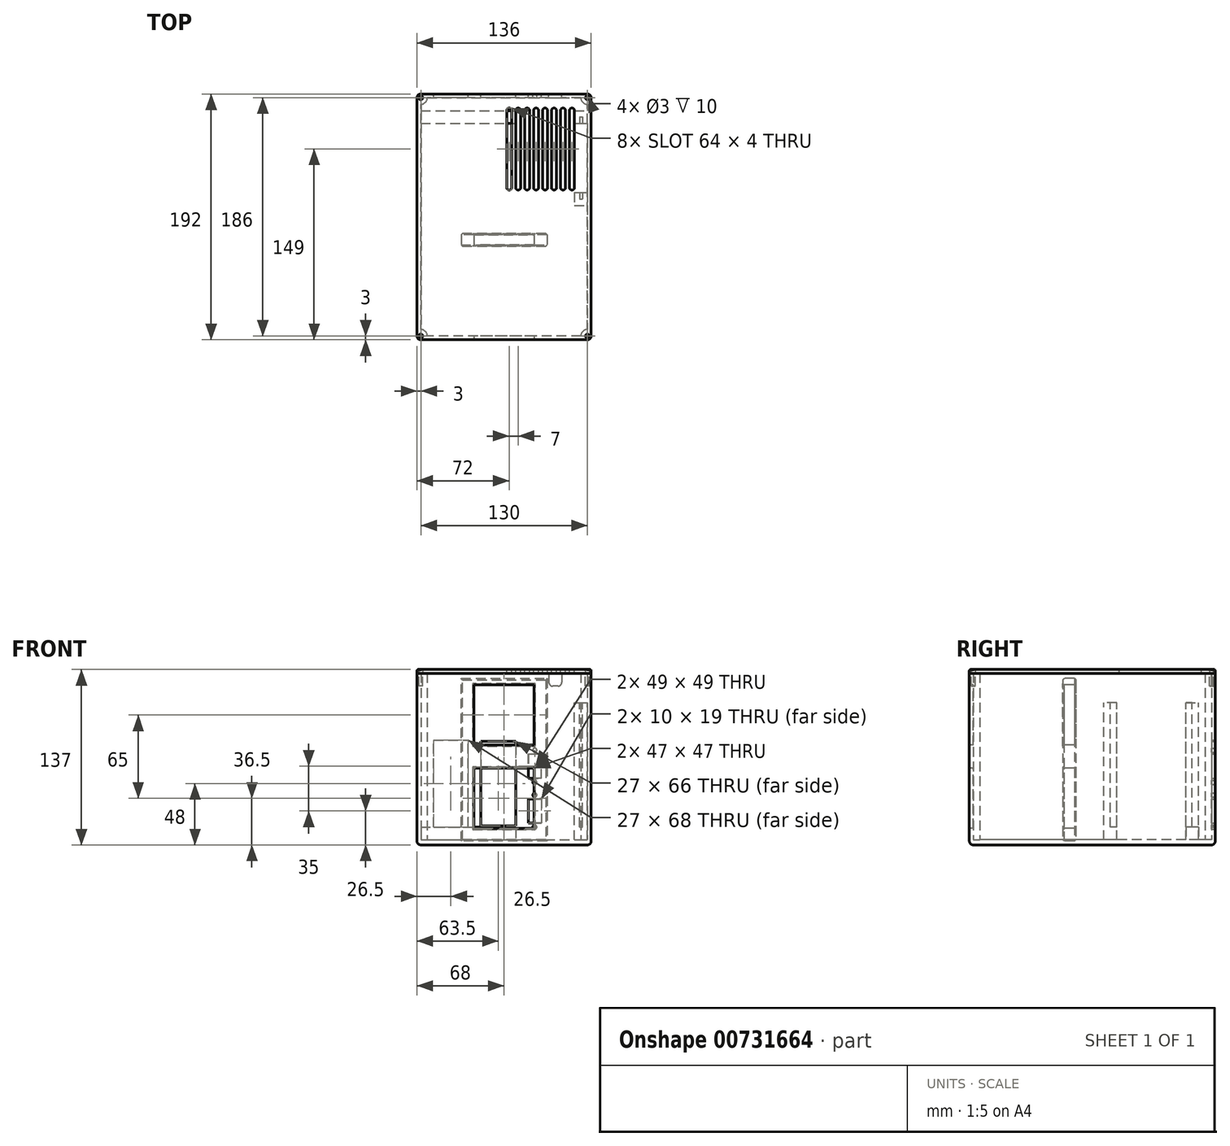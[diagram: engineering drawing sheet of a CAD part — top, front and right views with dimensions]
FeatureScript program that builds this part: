
annotation { "Feature Type Name" : "Feature", "Feature Type Description" : "" }
export const myFeature = defineFeature(function(context is Context, id is Id, definition is map)
    precondition{}
    {
        {
            var Q0;
            Q0=qCreatedBy(makeId("Top.planeOp"),FACE);
            var sketch = newSketch(context, id + "F0", { "sketchPlane" : qUnion([Q0])});
            skLineSegment(sketch, "E0.bottom", {"start": v(60, -93) * mm, "end": v(-60, -93) * mm});
            skLineSegment(sketch, "E0.top", {"start": v(60, 93) * mm, "end": v(-60, 93) * mm});
            skLineSegment(sketch, "E0.left", {"start": v(65, -88) * mm, "end": v(65, 88) * mm});
            skLineSegment(sketch, "E0.right", {"start": v(-65, -88) * mm, "end": v(-65, 88) * mm});
            skPoint(sketch, "E0.middle", {"position": v(0, 0) * mm});
            skLineSegment(sketch, "E1.bottom", {"start": v(68, -96) * mm, "end": v(-68, -96) * mm});
            skLineSegment(sketch, "E1.top", {"start": v(68, 96) * mm, "end": v(-68, 96) * mm});
            skLineSegment(sketch, "E1.left", {"start": v(68, -96) * mm, "end": v(68, 96) * mm});
            skLineSegment(sketch, "E1.right", {"start": v(-68, -96) * mm, "end": v(-68, 96) * mm});
            skArc(sketch, "E2", {"start": v(65, 88) * mm, "mid": v(61.46, 89.46) * mm, "end": v(60, 93) * mm});
            skArc(sketch, "E3.MirrorCS", {"start": v(65, -88) * mm, "mid": v(61.46, -89.46) * mm, "end": v(60, -93) * mm});
            skArc(sketch, "E4.MirrorCS", {"start": v(-65, -88) * mm, "mid": v(-61.46, -89.46) * mm, "end": v(-60, -93) * mm});
            skArc(sketch, "E5.MirrorCS", {"start": v(-65, 88) * mm, "mid": v(-61.46, 89.46) * mm, "end": v(-60, 93) * mm});
            skSolve(sketch);
        }
        {
            var Q0;
            Q0=makeQuery(id+"F0.imprint","IMPRINT",FACE,{"disambiguationData":[TD([[makeQuery(id+"F0.imprint","IMPRINT",EDGE,{"derivedFrom":sQuery(id+"F0.wireOp",EDGE,"E0.bottom")}),-1.0]])]});
            var Q1;
            Q1=makeQuery(id+"F0.imprint","IMPRINT",FACE,{"disambiguationData":[TD([[makeQuery(id+"F0.imprint","IMPRINT",EDGE,{"derivedFrom":sQuery(id+"F0.wireOp",EDGE,"E0.bottom")}),1.0]])]});
            extrude(context, id + "F1", {"entities" : qUnion([Q0, Q1]), "depth" : 4 * mm, "offsetDistance" : 25 * mm});
        }
        {
            var Q0;
            Q0=makeQuery(id+"F0.imprint","IMPRINT",FACE,{"disambiguationData":[TD([[makeQuery(id+"F0.imprint","IMPRINT",EDGE,{"derivedFrom":sQuery(id+"F0.wireOp",EDGE,"E0.bottom")}),1.0]])]});
            extrude(context, id + "F2", {"entities" : qUnion([Q0]), "operationType" : NewBodyOperationType.ADD, "depth" : 134 * mm, "offsetDistance" : 25 * mm});
        }
        {
            var Q0;
            {var subQ0=sQuery(id+"F0.wireOp",EDGE,"E1.bottom");Q0=makeQuery(id+"F2.boolean.opBoolean","MERGE",FACE,{"derivedFrom":[makeQuery(id+"F1.opExtrude","SWEPT_FACE",FACE,{"disambiguationData":[OSD([subQ0])]}),makeQuery(id+"F2.opExtrude","SWEPT_FACE",FACE,{"disambiguationData":[OSD([subQ0])]})]});}
            var sketch = newSketch(context, id + "F3", { "sketchPlane" : qUnion([Q0])});
            skLineSegment(sketch, "E6.bottom", {"start": v(23.5, 78) * mm, "end": v(-23.5, 78) * mm});
            skLineSegment(sketch, "E6.top", {"start": v(23.5, 125) * mm, "end": v(-23.5, 125) * mm});
            skLineSegment(sketch, "E6.left", {"start": v(23.5, 78) * mm, "end": v(23.5, 125) * mm});
            skLineSegment(sketch, "E6.right", {"start": v(-23.5, 78) * mm, "end": v(-23.5, 125) * mm});
            skPoint(sketch, "E6.middle", {"position": v(0, 101.5) * mm});
            skLineSegment(sketch, "E7.bottom", {"start": v(23.5, 13) * mm, "end": v(-23.5, 13) * mm});
            skLineSegment(sketch, "E7.top", {"start": v(23.5, 60) * mm, "end": v(-23.5, 60) * mm});
            skLineSegment(sketch, "E7.left", {"start": v(23.5, 13) * mm, "end": v(23.5, 60) * mm});
            skLineSegment(sketch, "E7.right", {"start": v(-23.5, 13) * mm, "end": v(-23.5, 60) * mm});
            skPoint(sketch, "E7.middle", {"position": v(0, 36.5) * mm});
            skSolve(sketch);
        }
        {
            var Q0;
            Q0=makeQuery(id+"F3.imprint","IMPRINT",FACE,{"disambiguationData":[TD([[makeQuery(id+"F3.imprint","IMPRINT",EDGE,{"derivedFrom":sQuery(id+"F3.wireOp",EDGE,"E6.bottom")}),-1.0]])]});
            var Q1;
            Q1=makeQuery(id+"F3.imprint","IMPRINT",FACE,{"disambiguationData":[TD([[makeQuery(id+"F3.imprint","IMPRINT",EDGE,{"derivedFrom":sQuery(id+"F3.wireOp",EDGE,"E7.bottom")}),-1.0]])]});
            extrude(context, id + "F4", {"entities" : qUnion([Q0, Q1]), "operationType" : NewBodyOperationType.REMOVE, "oppositeDirection" : true, "depth" : 25 * mm, "offsetDistance" : 25 * mm});
        }
        {
            var Q0;
            Q0=makeQuery(id+"F1.opExtrude","CAP_FACE",FACE,{"disambiguationData":[OSD([sQuery(id+"F0.wireOp",EDGE,"E1.bottom"),sQuery(id+"F0.wireOp",EDGE,"E1.top"),sQuery(id+"F0.wireOp",EDGE,"E1.left"),sQuery(id+"F0.wireOp",EDGE,"E1.right")])],"isStart":false});
            var sketch = newSketch(context, id + "F5", { "sketchPlane" : qUnion([Q0])});
            skLineSegment(sketch, "E8.bottom", {"start": v(-65, 73) * mm, "end": v(19, 73) * mm});
            skLineSegment(sketch, "E8.top", {"start": v(-65, 83) * mm, "end": v(19, 83) * mm});
            skLineSegment(sketch, "E8.left", {"start": v(-65, 73) * mm, "end": v(-65, 83) * mm});
            skLineSegment(sketch, "E8.right", {"start": v(19, 73) * mm, "end": v(19, 83) * mm});
            skSolve(sketch);
        }
        {
            var Q0;
            Q0=makeQuery(id+"F5.imprint","IMPRINT",FACE,{"disambiguationData":[TD([[makeQuery(id+"F5.imprint","IMPRINT",EDGE,{"derivedFrom":sQuery(id+"F5.wireOp",EDGE,"E8.bottom")}),1.0]])]});
            extrude(context, id + "F6", {"entities" : qUnion([Q0]), "operationType" : NewBodyOperationType.ADD, "depth" : 20 * mm, "offsetDistance" : 25 * mm});
        }
        {
            var Q0;
            Q0=makeQuery(id+"F6.opExtrude","SWEPT_FACE",FACE,{"disambiguationData":[OSD([sQuery(id+"F5.wireOp",EDGE,"E8.bottom")])]});
            var sketch = newSketch(context, id + "F7", { "sketchPlane" : qUnion([Q0])});
            skLineSegment(sketch, "E9", {"start": v(-18, 14) * mm, "end": v(9, 14) * mm});
            skLineSegment(sketch, "E10", {"start": v(-28, 14) * mm, "end": v(-55, 14) * mm});
            skLineSegment(sketch, "E11", {"start": v(-55, 33.64) * mm, "end": v(19, 33.64) * mm});
            skLineSegment(sketch, "E12", {"start": v(19, 33.64) * mm, "end": v(19, 24) * mm});
            skLineSegment(sketch, "E13", {"start": v(-28, 14) * mm, "end": v(-18, 14) * mm});
            skLineSegment(sketch, "E14.0.0", {"start": v(9, 4) * mm, "end": v(19, 4) * mm});
            skLineSegment(sketch, "E14.0.1", {"start": v(19, 4) * mm, "end": v(19, 24) * mm});
            skLineSegment(sketch, "E14.0.3", {"start": v(-65, 24) * mm, "end": v(-65, 14) * mm});
            skLineSegment(sketch, "E15", {"start": v(9, 14) * mm, "end": v(9, 4) * mm});
            skLineSegment(sketch, "E16", {"start": v(-55, 14) * mm, "end": v(-65, 14) * mm});
            skLineSegment(sketch, "E17", {"start": v(-65, 24) * mm, "end": v(-65, 33.64) * mm});
            skLineSegment(sketch, "E18", {"start": v(-65, 33.64) * mm, "end": v(-55, 33.64) * mm});
            skPoint(sketch, "E19.orphan", {"position": v(-65, 4) * mm});
            skSolve(sketch);
        }
        {
            var Q0;
            Q0=qSketchRegion(id+"F7",true);
            extrude(context, id + "F8", {"entities" : qUnion([Q0]), "operationType" : NewBodyOperationType.REMOVE, "oppositeDirection" : true, "depth" : 10 * mm, "offsetDistance" : 25 * mm});
        }
        {
            var Q0;
            Q0=makeQuery(id+"F2.opExtrude","SWEPT_FACE",FACE,{"disambiguationData":[OSD([sQuery(id+"F0.wireOp",EDGE,"E0.left")])]});
            var sketch = newSketch(context, id + "F9", { "sketchPlane" : qUnion([Q0])});
            skLineSegment(sketch, "E20.bottom", {"start": v(-73, 4) * mm, "end": v(-83, 4) * mm});
            skLineSegment(sketch, "E20.top", {"start": v(-73, 111) * mm, "end": v(-83, 111) * mm});
            skLineSegment(sketch, "E20.left", {"start": v(-73, 4) * mm, "end": v(-73, 111) * mm});
            skLineSegment(sketch, "E20.right", {"start": v(-83, 4) * mm, "end": v(-83, 111) * mm});
            skLineSegment(sketch, "E21.bottom", {"start": v(-19, 4) * mm, "end": v(-9, 4) * mm});
            skLineSegment(sketch, "E21.top", {"start": v(-19, 111) * mm, "end": v(-9, 111) * mm});
            skLineSegment(sketch, "E21.left", {"start": v(-19, 4) * mm, "end": v(-19, 111) * mm});
            skLineSegment(sketch, "E21.right", {"start": v(-9, 4) * mm, "end": v(-9, 111) * mm});
            skPoint(sketch, "E22.centerSnap0", {"position": v(-78, 111) * mm});
            skPoint(sketch, "E23.centerSnap0", {"position": v(-14, 111) * mm});
            skPoint(sketch, "E24.centerSnap0", {"position": v(-78, 4) * mm});
            skSolve(sketch);
        }
        {
            var Q0;
            Q0=qSketchRegion(id+"F9",true);
            extrude(context, id + "F10", {"entities" : qUnion([Q0]), "operationType" : NewBodyOperationType.ADD, "depth" : 10 * mm, "offsetDistance" : 25 * mm});
        }
        {
            var Q0;
            Q0=makeQuery(id+"F2.opExtrude","CAP_FACE",FACE,{"disambiguationData":[OSD([sQuery(id+"F0.wireOp",EDGE,"E0.bottom"),sQuery(id+"F0.wireOp",EDGE,"E0.top"),sQuery(id+"F0.wireOp",EDGE,"E0.left"),sQuery(id+"F0.wireOp",EDGE,"E0.right"),sQuery(id+"F0.wireOp",EDGE,"E1.bottom"),sQuery(id+"F0.wireOp",EDGE,"E1.top"),sQuery(id+"F0.wireOp",EDGE,"E1.left"),sQuery(id+"F0.wireOp",EDGE,"E1.right"),sQuery(id+"F0.wireOp",EDGE,"E2"),sQuery(id+"F0.wireOp",EDGE,"E3.MirrorCS"),sQuery(id+"F0.wireOp",EDGE,"E4.MirrorCS"),sQuery(id+"F0.wireOp",EDGE,"E5.MirrorCS")])],"isStart":false});
            var sketch = newSketch(context, id + "F11", { "sketchPlane" : qUnion([Q0])});
            skCircle(sketch, "E25", {"center": v(65, 93) * mm, "radius": 1.5 * mm});
            skCircle(sketch, "E26", {"center": v(-65, 93) * mm, "radius": 1.5 * mm});
            skCircle(sketch, "E27", {"center": v(65, -93) * mm, "radius": 1.5 * mm});
            skCircle(sketch, "E28", {"center": v(-65, -93) * mm, "radius": 1.5 * mm});
            skSolve(sketch);
        }
        {
            var Q0;
            Q0=qSketchRegion(id+"F11",true);
            extrude(context, id + "F12", {"entities" : qUnion([Q0]), "operationType" : NewBodyOperationType.REMOVE, "oppositeDirection" : true, "depth" : 10 * mm, "offsetDistance" : 25 * mm});
        }
        {
            var Q0;
            {var subQ0=sQuery(id+"F0.wireOp",EDGE,"E1.top");Q0=makeQuery(id+"F2.boolean.opBoolean","MERGE",FACE,{"derivedFrom":[makeQuery(id+"F1.opExtrude","SWEPT_FACE",FACE,{"disambiguationData":[OSD([subQ0])]}),makeQuery(id+"F2.opExtrude","SWEPT_FACE",FACE,{"disambiguationData":[OSD([subQ0])]})]});}
            var sketch = newSketch(context, id + "F13", { "sketchPlane" : qUnion([Q0])});
            skLineSegment(sketch, "E29.bottom", {"start": v(55, 14) * mm, "end": v(28, 14) * mm});
            skLineSegment(sketch, "E29.top", {"start": v(55, 82) * mm, "end": v(28, 82) * mm});
            skLineSegment(sketch, "E29.left", {"start": v(55, 14) * mm, "end": v(55, 82) * mm});
            skLineSegment(sketch, "E29.right", {"start": v(28, 14) * mm, "end": v(28, 82) * mm});
            skPoint(sketch, "E29.middle", {"position": v(41.5, 48) * mm});
            skLineSegment(sketch, "E30.bottom", {"start": v(18, 15) * mm, "end": v(-9, 15) * mm});
            skLineSegment(sketch, "E30.top", {"start": v(18, 81) * mm, "end": v(-9, 81) * mm});
            skLineSegment(sketch, "E30.left", {"start": v(18, 15) * mm, "end": v(18, 81) * mm});
            skLineSegment(sketch, "E30.right", {"start": v(-9, 15) * mm, "end": v(-9, 81) * mm});
            skPoint(sketch, "E30.middle", {"position": v(4.5, 48) * mm});
            skLineSegment(sketch, "E31.bottom", {"start": v(-45, 134) * mm, "end": v(-35, 134) * mm});
            skLineSegment(sketch, "E31.top", {"start": v(-45, 124) * mm, "end": v(-35, 124) * mm});
            skLineSegment(sketch, "E31.left", {"start": v(-45, 134) * mm, "end": v(-45, 124) * mm});
            skLineSegment(sketch, "E31.right", {"start": v(-35, 134) * mm, "end": v(-35, 124) * mm});
            skLineSegment(sketch, "E32.bottom", {"start": v(-29, 36) * mm, "end": v(-19, 36) * mm});
            skLineSegment(sketch, "E32.top", {"start": v(-29, 17) * mm, "end": v(-19, 17) * mm});
            skLineSegment(sketch, "E32.left", {"start": v(-29, 36) * mm, "end": v(-29, 17) * mm});
            skLineSegment(sketch, "E32.right", {"start": v(-19, 36) * mm, "end": v(-19, 17) * mm});
            skCircle(sketch, "E33", {"center": v(-24, 14) * mm, "radius": 1.6 * mm});
            skPoint(sketch, "E33.centerSnap0", {"position": v(-24, 17) * mm});
            skCircle(sketch, "E34", {"center": v(-24, 39) * mm, "radius": 1.6 * mm});
            skPoint(sketch, "E34.centerSnap0", {"position": v(-24, 36) * mm});
            skCircle(sketch, "E35", {"center": v(-24, 49) * mm, "radius": 1.6 * mm});
            skLineSegment(sketch, "E36.bottom", {"start": v(-19, 52) * mm, "end": v(-29, 52) * mm});
            skLineSegment(sketch, "E36.top", {"start": v(-19, 71) * mm, "end": v(-29, 71) * mm});
            skLineSegment(sketch, "E36.left", {"start": v(-19, 52) * mm, "end": v(-19, 71) * mm});
            skLineSegment(sketch, "E36.right", {"start": v(-29, 52) * mm, "end": v(-29, 71) * mm});
            skCircle(sketch, "E37", {"center": v(-24, 74) * mm, "radius": 1.6 * mm});
            skSolve(sketch);
        }
        {
            var Q0;
            Q0=makeQuery(id+"F13.imprint","IMPRINT",FACE,{"disambiguationData":[TD([[makeQuery(id+"F13.imprint","IMPRINT",EDGE,{"derivedFrom":sQuery(id+"F13.wireOp",EDGE,"E31.bottom")}),-1.0]])]});
            var Q1;
            Q1=qSketchRegion(id+"F13",true);
            extrude(context, id + "F14", {"entities" : qUnion([Q0, Q1]), "operationType" : NewBodyOperationType.REMOVE, "oppositeDirection" : true, "depth" : 25 * mm, "offsetDistance" : 25 * mm});
        }
        {
            var Q0;
            {var subQ0=sQuery(id+"F0.wireOp",EDGE,"E1.right");var subQ1=sQuery(id+"F0.wireOp",EDGE,"E1.bottom");Q0=makeQuery(id+"F2.boolean.opBoolean","MERGE",EDGE,{"derivedFrom":[makeQuery(id+"F1.opExtrude","SWEPT_EDGE",EDGE,{"disambiguationData":[OSD([subQ1,subQ0])]}),makeQuery(id+"F2.opExtrude","SWEPT_EDGE",EDGE,{"disambiguationData":[OSD([subQ1,subQ0])]})]});}
            var Q1;
            {var subQ0=sQuery(id+"F0.wireOp",EDGE,"E1.left");var subQ1=sQuery(id+"F0.wireOp",EDGE,"E1.bottom");Q1=makeQuery(id+"F2.boolean.opBoolean","MERGE",EDGE,{"derivedFrom":[makeQuery(id+"F1.opExtrude","SWEPT_EDGE",EDGE,{"disambiguationData":[OSD([subQ1,subQ0])]}),makeQuery(id+"F2.opExtrude","SWEPT_EDGE",EDGE,{"disambiguationData":[OSD([subQ1,subQ0])]})]});}
            var Q2;
            {var subQ0=sQuery(id+"F0.wireOp",EDGE,"E1.left");var subQ1=sQuery(id+"F0.wireOp",EDGE,"E1.top");Q2=makeQuery(id+"F2.boolean.opBoolean","MERGE",EDGE,{"derivedFrom":[makeQuery(id+"F1.opExtrude","SWEPT_EDGE",EDGE,{"disambiguationData":[OSD([subQ1,subQ0])]}),makeQuery(id+"F2.opExtrude","SWEPT_EDGE",EDGE,{"disambiguationData":[OSD([subQ1,subQ0])]})]});}
            var Q3;
            {var subQ0=sQuery(id+"F0.wireOp",EDGE,"E1.right");var subQ1=sQuery(id+"F0.wireOp",EDGE,"E1.top");Q3=makeQuery(id+"F2.boolean.opBoolean","MERGE",EDGE,{"derivedFrom":[makeQuery(id+"F1.opExtrude","SWEPT_EDGE",EDGE,{"disambiguationData":[OSD([subQ1,subQ0])]}),makeQuery(id+"F2.opExtrude","SWEPT_EDGE",EDGE,{"disambiguationData":[OSD([subQ1,subQ0])]})]});}
            fillet(context, id + "F15", {"entities" : qUnion([Q0, Q1, Q2, Q3]), "radius" : 3 * mm, "tangentPropagation" : true, "allowEdgeOverflow" : false});
        }
        {
            var Q0;
            Q0=makeQuery(id+"F1.opExtrude","CAP_EDGE",EDGE,{"disambiguationData":[OSD([sQuery(id+"F0.wireOp",EDGE,"E1.bottom")])],"isStart":true});
            fillet(context, id + "F16", {"entities" : qUnion([Q0]), "radius" : 3 * mm, "tangentPropagation" : true, "allowEdgeOverflow" : false});
        }
        {
            var Q0;
            Q0=makeQuery(id+"F14.boolean.opBoolean","COPY",EDGE,{"derivedFrom":makeQuery(id+"F14.opExtrude","SWEPT_EDGE",EDGE,{"disambiguationData":[OSD([sQuery(id+"F13.wireOp",EDGE,"E31.top"),sQuery(id+"F13.wireOp",EDGE,"E31.left")])]})});
            var Q1;
            Q1=makeQuery(id+"F14.boolean.opBoolean","COPY",EDGE,{"derivedFrom":makeQuery(id+"F14.opExtrude","SWEPT_EDGE",EDGE,{"disambiguationData":[OSD([sQuery(id+"F13.wireOp",EDGE,"E31.top"),sQuery(id+"F13.wireOp",EDGE,"E31.right")])]})});
            fillet(context, id + "F17", {"entities" : qUnion([Q0, Q1]), "radius" : 3 * mm, "tangentPropagation" : true, "allowEdgeOverflow" : false});
        }
        {
            var Q0;
            Q0=makeQuery(id+"F2.opExtrude","SWEPT_FACE",FACE,{"disambiguationData":[OSD([sQuery(id+"F0.wireOp",EDGE,"E0.bottom")])]});
            cPlane(context, id + "F18", {"entities" : qUnion([Q0]), "cplaneType" : CPlaneType.OFFSET, "offset" : 70 * mm, "width" : 150 * mm, "height" : 150 * mm});
        }
        {
            var Q0;
            Q0=qCreatedBy(id+"F18.planeOp",FACE);
            var sketch = newSketch(context, id + "F19", { "sketchPlane" : qUnion([Q0])});
            skLineSegment(sketch, "E38.0", {"start": v(-23.5, 125) * mm, "end": v(23.5, 125) * mm});
            skLineSegment(sketch, "E39.0", {"start": v(-23.5, 78) * mm, "end": v(-23.5, 125) * mm});
            skLineSegment(sketch, "E40.0", {"start": v(23.5, 78) * mm, "end": v(23.5, 125) * mm});
            skLineSegment(sketch, "E41.0", {"start": v(-23.5, 78) * mm, "end": v(23.5, 78) * mm});
            skLineSegment(sketch, "E42.0", {"start": v(-23.5, 60) * mm, "end": v(23.5, 60) * mm});
            skLineSegment(sketch, "E43.0", {"start": v(23.5, 13) * mm, "end": v(23.5, 60) * mm});
            skLineSegment(sketch, "E44.0", {"start": v(-23.5, 13) * mm, "end": v(23.5, 13) * mm});
            skLineSegment(sketch, "E45.0", {"start": v(-23.5, 13) * mm, "end": v(-23.5, 60) * mm});
            skLineSegment(sketch, "E46.top", {"start": v(33.5, 130) * mm, "end": v(-33.5, 130) * mm});
            skLineSegment(sketch, "E46.left", {"start": v(33.5, 3) * mm, "end": v(33.5, 130) * mm});
            skLineSegment(sketch, "E46.right", {"start": v(-33.5, 3) * mm, "end": v(-33.5, 130) * mm});
            skLineSegment(sketch, "E47", {"start": v(-33.5, 3) * mm, "end": v(33.5, 3) * mm});
            skSolve(sketch);
        }
        {
            var Q0;
            Q0=makeQuery(id+"F19.imprint","IMPRINT",FACE,{"disambiguationData":[TD([[makeQuery(id+"F19.imprint","IMPRINT",EDGE,{"derivedFrom":sQuery(id+"F19.wireOp",EDGE,"E38.0")}),1.0]])]});
            extrude(context, id + "F20", {"entities" : qUnion([Q0]), "depth" : 10 * mm, "offsetDistance" : 25 * mm});
        }
        {
            var Q0;
            Q0=makeQuery(id+"F20.opExtrude","CAP_FACE",FACE,{"disambiguationData":[OSD([sQuery(id+"F19.wireOp",EDGE,"E38.0"),sQuery(id+"F19.wireOp",EDGE,"E39.0"),sQuery(id+"F19.wireOp",EDGE,"E40.0"),sQuery(id+"F19.wireOp",EDGE,"E41.0"),sQuery(id+"F19.wireOp",EDGE,"E42.0"),sQuery(id+"F19.wireOp",EDGE,"E43.0"),sQuery(id+"F19.wireOp",EDGE,"E44.0"),sQuery(id+"F19.wireOp",EDGE,"E45.0"),sQuery(id+"F19.wireOp",EDGE,"E46.top"),sQuery(id+"F19.wireOp",EDGE,"E46.left"),sQuery(id+"F19.wireOp",EDGE,"E46.right"),sQuery(id+"F19.wireOp",EDGE,"E47")])],"isStart":true});
            var Q1;
            Q1=makeQuery(id+"F20.opExtrude","CAP_FACE",FACE,{"disambiguationData":[OSD([sQuery(id+"F19.wireOp",EDGE,"E38.0"),sQuery(id+"F19.wireOp",EDGE,"E39.0"),sQuery(id+"F19.wireOp",EDGE,"E40.0"),sQuery(id+"F19.wireOp",EDGE,"E41.0"),sQuery(id+"F19.wireOp",EDGE,"E42.0"),sQuery(id+"F19.wireOp",EDGE,"E43.0"),sQuery(id+"F19.wireOp",EDGE,"E44.0"),sQuery(id+"F19.wireOp",EDGE,"E45.0"),sQuery(id+"F19.wireOp",EDGE,"E46.top"),sQuery(id+"F19.wireOp",EDGE,"E46.left"),sQuery(id+"F19.wireOp",EDGE,"E46.right"),sQuery(id+"F19.wireOp",EDGE,"E47")])],"isStart":false});
            chamfer(context, id + "F21", {"entities" : qUnion([Q0, Q1]), "width" : 1 * mm, "tangentPropagation" : true});
        }
        {
            var Q0;
            Q0=makeQuery(id+"F2.opExtrude","CAP_FACE",FACE,{"disambiguationData":[OSD([sQuery(id+"F0.wireOp",EDGE,"E0.bottom"),sQuery(id+"F0.wireOp",EDGE,"E0.top"),sQuery(id+"F0.wireOp",EDGE,"E0.left"),sQuery(id+"F0.wireOp",EDGE,"E0.right"),sQuery(id+"F0.wireOp",EDGE,"E1.bottom"),sQuery(id+"F0.wireOp",EDGE,"E1.top"),sQuery(id+"F0.wireOp",EDGE,"E1.left"),sQuery(id+"F0.wireOp",EDGE,"E1.right"),sQuery(id+"F0.wireOp",EDGE,"E2"),sQuery(id+"F0.wireOp",EDGE,"E3.MirrorCS"),sQuery(id+"F0.wireOp",EDGE,"E4.MirrorCS"),sQuery(id+"F0.wireOp",EDGE,"E5.MirrorCS")])],"isStart":false});
            cPlane(context, id + "F22", {"entities" : qUnion([Q0]), "cplaneType" : CPlaneType.OFFSET, "offset" : 0 * mm, "width" : 150 * mm, "height" : 150 * mm});
        }
        {
            var Q0;
            Q0=qCreatedBy(id+"F22.planeOp",FACE);
            var sketch = newSketch(context, id + "F23", { "sketchPlane" : qUnion([Q0])});
            skLineSegment(sketch, "E48.0.0", {"start": v(68, -93) * mm, "end": v(68, 93) * mm});
            skArc(sketch, "E48.0.1", {"start": v(68, 93) * mm, "mid": v(67.12, 95.12) * mm, "end": v(65, 96) * mm});
            skArc(sketch, "E48.0.5", {"start": v(60, 93) * mm, "mid": v(61.46, 89.46) * mm, "end": v(65, 88) * mm});
            skLineSegment(sketch, "E48.0.6", {"start": v(65, 88) * mm, "end": v(65, -88) * mm});
            skArc(sketch, "E48.0.7", {"start": v(65, -88) * mm, "mid": v(61.46, -89.46) * mm, "end": v(60, -93) * mm});
            skLineSegment(sketch, "E48.0.8", {"start": v(60, -93) * mm, "end": v(-60, -93) * mm});
            skArc(sketch, "E48.0.9", {"start": v(-60, -93) * mm, "mid": v(-61.46, -89.46) * mm, "end": v(-65, -88) * mm});
            skLineSegment(sketch, "E48.0.10", {"start": v(-65, -88) * mm, "end": v(-65, 88) * mm});
            skArc(sketch, "E48.0.11", {"start": v(-65, 88) * mm, "mid": v(-61.46, 89.46) * mm, "end": v(-60, 93) * mm});
            skLineSegment(sketch, "E48.0.12", {"start": v(-60, 93) * mm, "end": v(60, 93) * mm});
            skLineSegment(sketch, "E48.0.14", {"start": v(65, 96) * mm, "end": v(-65, 96) * mm});
            skArc(sketch, "E48.0.15", {"start": v(-65, 96) * mm, "mid": v(-67.12, 95.12) * mm, "end": v(-68, 93) * mm});
            skLineSegment(sketch, "E48.0.16", {"start": v(-68, 93) * mm, "end": v(-68, -93) * mm});
            skArc(sketch, "E48.0.17", {"start": v(-68, -93) * mm, "mid": v(-67.12, -95.12) * mm, "end": v(-65, -96) * mm});
            skLineSegment(sketch, "E48.0.18", {"start": v(-65, -96) * mm, "end": v(65, -96) * mm});
            skArc(sketch, "E48.0.19", {"start": v(65, -96) * mm, "mid": v(67.12, -95.12) * mm, "end": v(68, -93) * mm});
            skPoint(sketch, "E48.0.4.start.orphan", {"position": v(45, 93) * mm});
            skPoint(sketch, "E48.0.2.end.orphan", {"position": v(45, 96) * mm});
            skPoint(sketch, "E49.orphan", {"position": v(35, 93) * mm});
            skPoint(sketch, "E50.orphan", {"position": v(35, 96) * mm});
            skCircle(sketch, "E51.0", {"center": v(65, 93) * mm, "radius": 1.5 * mm});
            skCircle(sketch, "E52.0", {"center": v(-65, 93) * mm, "radius": 1.5 * mm});
            skCircle(sketch, "E53.0", {"center": v(65, -93) * mm, "radius": 1.5 * mm});
            skCircle(sketch, "E54.0", {"center": v(-65, -93) * mm, "radius": 1.5 * mm});
            skLineSegment(sketch, "E55.0", {"start": v(64, -87.08) * mm, "end": v(64, 87.08) * mm});
            skArc(sketch, "E55.1", {"start": v(59.08, -92) * mm, "mid": v(60.76, -88.76) * mm, "end": v(64, -87.08) * mm});
            skArc(sketch, "E55.2", {"start": v(64, 87.08) * mm, "mid": v(60.76, 88.76) * mm, "end": v(59.08, 92) * mm});
            skLineSegment(sketch, "E55.3", {"start": v(-59.08, -92) * mm, "end": v(59.08, -92) * mm});
            skLineSegment(sketch, "E55.4", {"start": v(59.08, 92) * mm, "end": v(-59.08, 92) * mm});
            skArc(sketch, "E55.5", {"start": v(-59.08, 92) * mm, "mid": v(-60.76, 88.76) * mm, "end": v(-64, 87.08) * mm});
            skLineSegment(sketch, "E55.6", {"start": v(-64, 87.08) * mm, "end": v(-64, -87.08) * mm});
            skArc(sketch, "E55.7", {"start": v(-64, -87.08) * mm, "mid": v(-60.76, -88.76) * mm, "end": v(-59.08, -92) * mm});
            skSolve(sketch);
        }
        {
            var Q0;
            Q0=makeQuery(id+"F23.imprint","IMPRINT",FACE,{"disambiguationData":[TD([[makeQuery(id+"F23.imprint","IMPRINT",EDGE,{"derivedFrom":sQuery(id+"F23.wireOp",EDGE,"E48.0.0")}),1.0]])]});
            var Q1;
            Q1=makeQuery(id+"F23.imprint","IMPRINT",FACE,{"disambiguationData":[TD([[makeQuery(id+"F23.imprint","IMPRINT",EDGE,{"derivedFrom":sQuery(id+"F23.wireOp",EDGE,"E48.0.5")}),-1.0]])]});
            var Q2;
            Q2=makeQuery(id+"F23.imprint","IMPRINT",FACE,{"disambiguationData":[TD([[makeQuery(id+"F23.imprint","IMPRINT",EDGE,{"derivedFrom":sQuery(id+"F23.wireOp",EDGE,"E55.0")}),1.0]])]});
            extrude(context, id + "F24", {"entities" : qUnion([Q0, Q1, Q2]), "depth" : 3 * mm, "offsetDistance" : 25 * mm});
        }
        {
            var Q0;
            Q0=makeQuery(id+"F24.opExtrude","CAP_FACE",FACE,{"disambiguationData":[OSD([sQuery(id+"F23.wireOp",EDGE,"E48.0.0"),sQuery(id+"F23.wireOp",EDGE,"E48.0.1"),sQuery(id+"F23.wireOp",EDGE,"E48.0.14"),sQuery(id+"F23.wireOp",EDGE,"E48.0.15"),sQuery(id+"F23.wireOp",EDGE,"E48.0.16"),sQuery(id+"F23.wireOp",EDGE,"E48.0.17"),sQuery(id+"F23.wireOp",EDGE,"E48.0.18"),sQuery(id+"F23.wireOp",EDGE,"E48.0.19"),sQuery(id+"F23.wireOp",EDGE,"E51.0"),sQuery(id+"F23.wireOp",EDGE,"E52.0"),sQuery(id+"F23.wireOp",EDGE,"E53.0"),sQuery(id+"F23.wireOp",EDGE,"E54.0")])],"isStart":false});
            fillet(context, id + "F25", {"entities" : qUnion([Q0]), "radius" : 1 * mm, "tangentPropagation" : true, "allowEdgeOverflow" : false});
        }
        {
            var Q0;
            Q0=makeQuery(id+"F24.opExtrude","CAP_FACE",FACE,{"disambiguationData":[OSD([sQuery(id+"F23.wireOp",EDGE,"E48.0.0"),sQuery(id+"F23.wireOp",EDGE,"E48.0.1"),sQuery(id+"F23.wireOp",EDGE,"E48.0.14"),sQuery(id+"F23.wireOp",EDGE,"E48.0.15"),sQuery(id+"F23.wireOp",EDGE,"E48.0.16"),sQuery(id+"F23.wireOp",EDGE,"E48.0.17"),sQuery(id+"F23.wireOp",EDGE,"E48.0.18"),sQuery(id+"F23.wireOp",EDGE,"E48.0.19"),sQuery(id+"F23.wireOp",EDGE,"E51.0"),sQuery(id+"F23.wireOp",EDGE,"E52.0"),sQuery(id+"F23.wireOp",EDGE,"E53.0"),sQuery(id+"F23.wireOp",EDGE,"E54.0")])],"isStart":false});
            var sketch = newSketch(context, id + "F26", { "sketchPlane" : qUnion([Q0])});
            skLineSegment(sketch, "E56.left", {"start": v(2, 83) * mm, "end": v(2, 23) * mm});
            skLineSegment(sketch, "E56.right", {"start": v(6, 83) * mm, "end": v(6, 23) * mm});
            skArc(sketch, "E57", {"start": v(2, 83) * mm, "mid": v(4, 85) * mm, "end": v(6, 83) * mm});
            skArc(sketch, "E58", {"start": v(2, 23) * mm, "mid": v(4, 21) * mm, "end": v(6, 23) * mm});
            skLineSegment(sketch, "E59.1.0.0", {"start": v(13, 83) * mm, "end": v(13, 23) * mm});
            skLineSegment(sketch, "E59.1.0.1", {"start": v(9, 83) * mm, "end": v(9, 23) * mm});
            skArc(sketch, "E59.1.0.2", {"start": v(9, 83) * mm, "mid": v(11, 85) * mm, "end": v(13, 83) * mm});
            skArc(sketch, "E59.1.0.3", {"start": v(9, 23) * mm, "mid": v(11, 21) * mm, "end": v(13, 23) * mm});
            skLineSegment(sketch, "E59.2.0.0", {"start": v(20, 83) * mm, "end": v(20, 23) * mm});
            skLineSegment(sketch, "E59.2.0.1", {"start": v(16, 83) * mm, "end": v(16, 23) * mm});
            skArc(sketch, "E59.2.0.2", {"start": v(16, 83) * mm, "mid": v(18, 85) * mm, "end": v(20, 83) * mm});
            skArc(sketch, "E59.2.0.3", {"start": v(16, 23) * mm, "mid": v(18, 21) * mm, "end": v(20, 23) * mm});
            skLineSegment(sketch, "E59.3.0.0", {"start": v(27, 83) * mm, "end": v(27, 23) * mm});
            skLineSegment(sketch, "E59.3.0.1", {"start": v(23, 83) * mm, "end": v(23, 23) * mm});
            skArc(sketch, "E59.3.0.2", {"start": v(23, 83) * mm, "mid": v(25, 85) * mm, "end": v(27, 83) * mm});
            skArc(sketch, "E59.3.0.3", {"start": v(23, 23) * mm, "mid": v(25, 21) * mm, "end": v(27, 23) * mm});
            skLineSegment(sketch, "E59.4.0.0", {"start": v(34, 83) * mm, "end": v(34, 23) * mm});
            skLineSegment(sketch, "E59.4.0.1", {"start": v(30, 83) * mm, "end": v(30, 23) * mm});
            skArc(sketch, "E59.4.0.2", {"start": v(30, 83) * mm, "mid": v(32, 85) * mm, "end": v(34, 83) * mm});
            skArc(sketch, "E59.4.0.3", {"start": v(30, 23) * mm, "mid": v(32, 21) * mm, "end": v(34, 23) * mm});
            skLineSegment(sketch, "E59.5.0.0", {"start": v(41, 83) * mm, "end": v(41, 23) * mm});
            skLineSegment(sketch, "E59.5.0.1", {"start": v(37, 83) * mm, "end": v(37, 23) * mm});
            skArc(sketch, "E59.5.0.2", {"start": v(37, 83) * mm, "mid": v(39, 85) * mm, "end": v(41, 83) * mm});
            skArc(sketch, "E59.5.0.3", {"start": v(37, 23) * mm, "mid": v(39, 21) * mm, "end": v(41, 23) * mm});
            skLineSegment(sketch, "E59.6.0.0", {"start": v(48, 83) * mm, "end": v(48, 23) * mm});
            skLineSegment(sketch, "E59.6.0.1", {"start": v(44, 83) * mm, "end": v(44, 23) * mm});
            skArc(sketch, "E59.6.0.2", {"start": v(44, 83) * mm, "mid": v(46, 85) * mm, "end": v(48, 83) * mm});
            skArc(sketch, "E59.6.0.3", {"start": v(44, 23) * mm, "mid": v(46, 21) * mm, "end": v(48, 23) * mm});
            skLineSegment(sketch, "E59.7.0.0", {"start": v(55, 83) * mm, "end": v(55, 23) * mm});
            skLineSegment(sketch, "E59.7.0.1", {"start": v(51, 83) * mm, "end": v(51, 23) * mm});
            skArc(sketch, "E59.7.0.2", {"start": v(51, 83) * mm, "mid": v(53, 85) * mm, "end": v(55, 83) * mm});
            skArc(sketch, "E59.7.0.3", {"start": v(51, 23) * mm, "mid": v(53, 21) * mm, "end": v(55, 23) * mm});
            skLineSegment(sketch, "E59.direction1", {"start": v(2, 23) * mm, "end": v(9, 23) * mm, "construction": true});
            skLineSegment(sketch, "E59.direction2", {"start": v(2, 23) * mm, "end": v(2, 23) * mm});
            skSolve(sketch);
        }
        {
            var Q0;
            Q0=qSketchRegion(id+"F26",true);
            extrude(context, id + "F27", {"entities" : qUnion([Q0]), "operationType" : NewBodyOperationType.REMOVE, "oppositeDirection" : true, "depth" : 25 * mm, "offsetDistance" : 25 * mm});
        }
        {
            var Q0;
            Q0=makeQuery(id+"F10.opExtrude","SWEPT_FACE",FACE,{"disambiguationData":[OSD([sQuery(id+"F9.wireOp",EDGE,"E21.top")])]});
            var sketch = newSketch(context, id + "F28", { "sketchPlane" : qUnion([Q0])});
            skLineSegment(sketch, "E60.bottom", {"start": v(58.9, 78) * mm, "end": v(61.1, 78) * mm});
            skLineSegment(sketch, "E60.top", {"start": v(58.9, 14) * mm, "end": v(61.1, 14) * mm});
            skLineSegment(sketch, "E60.left", {"start": v(58.9, 78) * mm, "end": v(58.9, 14) * mm});
            skLineSegment(sketch, "E60.right", {"start": v(61.1, 78) * mm, "end": v(61.1, 14) * mm});
            skSolve(sketch);
        }
        {
            var Q0;
            {var subQ0=sQuery(id+"F28.wireOp",EDGE,"E60.bottom");Q0=makeQuery(id+"F28.imprint","IMPRINT",FACE,{"disambiguationData":[TD([[makeQuery(id+"F28.imprint","IMPRINT",EDGE,{"derivedFrom":subQ0}),-1.0]])]});}
            var Q1;
            {var subQ0=sQuery(id+"F28.wireOp",EDGE,"E60.top");Q1=makeQuery(id+"F28.imprint","IMPRINT",FACE,{"disambiguationData":[TD([[makeQuery(id+"F28.imprint","IMPRINT",EDGE,{"derivedFrom":subQ0}),1.0]])]});}
            extrude(context, id + "F29", {"entities" : qUnion([Q0, Q1]), "operationType" : NewBodyOperationType.REMOVE, "oppositeDirection" : true, "depth" : 97 * mm, "offsetDistance" : 25 * mm});
        }
    });
